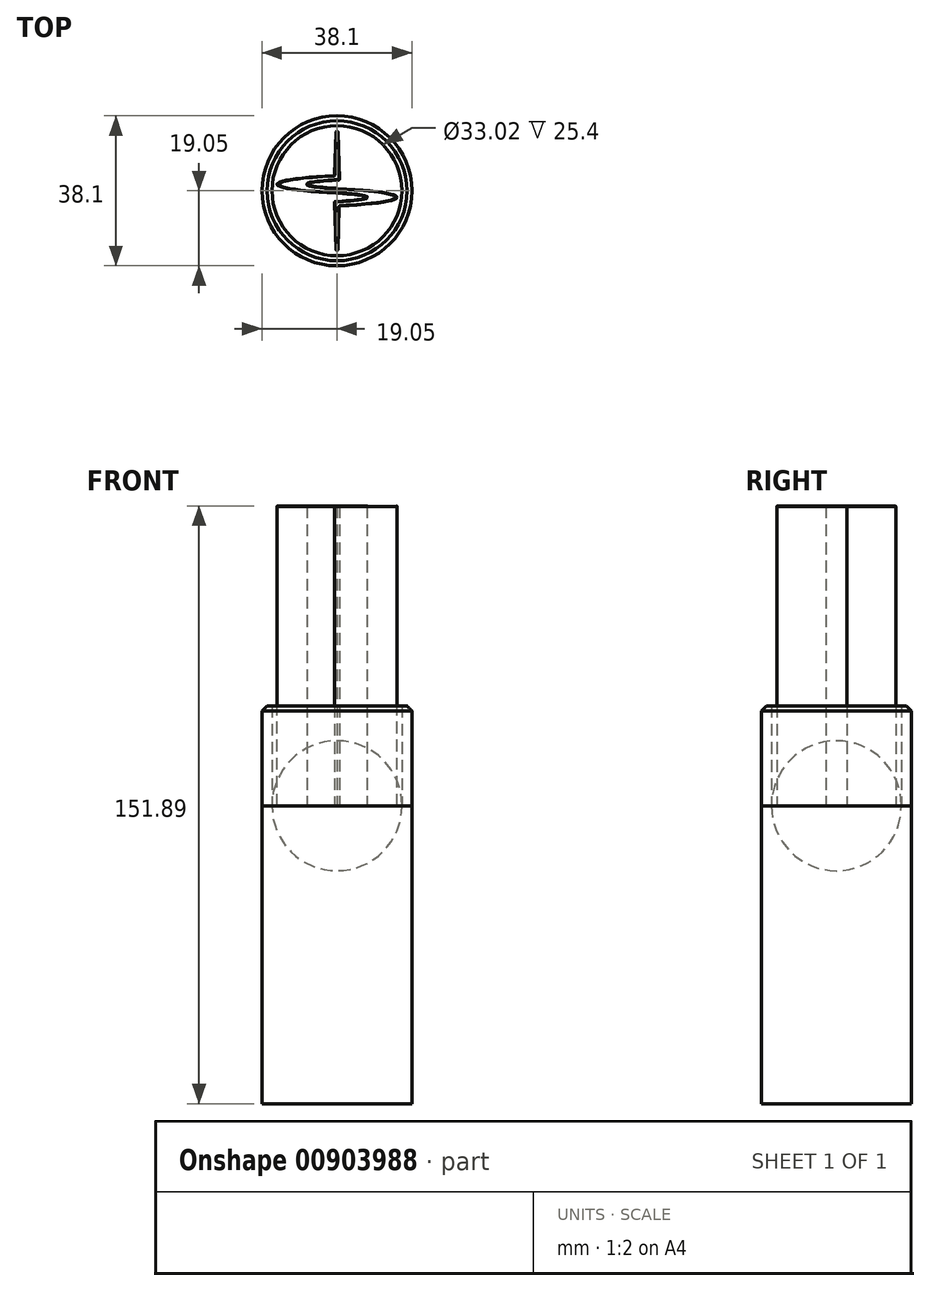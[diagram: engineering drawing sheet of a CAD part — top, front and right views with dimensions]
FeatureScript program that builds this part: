
annotation { "Feature Type Name" : "Feature", "Feature Type Description" : "" }
export const myFeature = defineFeature(function(context is Context, id is Id, definition is map)
    precondition{}
    {
        {
            var Q0;
            Q0=qCreatedBy(makeId("Top.planeOp"),FACE);
            var sketch = newSketch(context, id + "F0", { "sketchPlane" : qUnion([Q0])});
            skEllipticalArc(sketch, "E0", {});
            skEllipticalArc(sketch, "E1", {});
            skLineSegment(sketch, "E2", {"start": v(0, 0.6) * mm, "end": v(0, -0.6) * mm});
            skLineSegment(sketch, "E3", {"start": v(0, 3.92) * mm, "end": v(0, 2.71) * mm});
            const initialGuessF0  = {"E0": [0.0127, 0.0016577330848633332, -1, 0, 0.02794, 0.00254, 5.184250817664331, 1.0989344895152549], "E1": [0.0381, 0.0016577330848633332, -1, 0, 0.04572, 0.001905, 5.697499763722436, 0.5856855434571507]};
            skSetInitialGuess(sketch, initialGuessF0);
            skSolve(sketch);
        }
        {
            var Q0;
            Q0=qCreatedBy(makeId("Top.planeOp"),FACE);
            var sketch = newSketch(context, id + "F1", { "sketchPlane" : qUnion([Q0])});
            skLineSegment(sketch, "E4", {"start": v(-0.63, 2.71) * mm, "end": v(0.63, 2.71) * mm});
            skLineSegment(sketch, "E5", {"start": v(0.64, 2.71) * mm, "end": v(0, 23.03) * mm});
            skLineSegment(sketch, "E6", {"start": v(0, 23.03) * mm, "end": v(-0.64, 2.71) * mm});
            skSolve(sketch);
        }
        {
            var Q0;
            Q0=makeQuery(id+"F0.imprint","IMPRINT",FACE,{"disambiguationData":[TD([[makeQuery(id+"F0.imprint","IMPRINT",EDGE,{"derivedFrom":sQuery(id+"F0.wireOp",EDGE,"E0")}),1.0]])]});
            var Q1;
            Q1=makeQuery(id+"F1.imprint","IMPRINT",FACE,{"disambiguationData":[TD([[makeQuery(id+"F1.imprint","IMPRINT",EDGE,{"derivedFrom":sQuery(id+"F1.wireOp",EDGE,"E4")}),1.0]])]});
            extrude(context, id + "F2", {"entities" : qUnion([Q0, Q1]), "depth" : 76.2 * mm, "offsetDistance" : 25.4 * mm});
        }
        {
            var Q0;
            Q0=qCreatedBy(makeId("Front.planeOp"),FACE);
            var sketch = newSketch(context, id + "F3", { "sketchPlane" : qUnion([Q0])});
            skLineSegment(sketch, "E7", {"start": v(0, 85.95) * mm, "end": v(0, -92.06) * mm});
            skSolve(sketch);
        }
        {
            var Q0;
            Q0=makeQuery(id+"F2.opExtrude","SWEPT_BODY",BODY,{"disambiguationData":[OSD([sQuery(id+"F1.wireOp",EDGE,"E4"),sQuery(id+"F1.wireOp",EDGE,"E5"),sQuery(id+"F1.wireOp",EDGE,"E6")])]});
            var Q1;
            Q1=makeQuery(id+"F2.opExtrude","SWEPT_BODY",BODY,{"disambiguationData":[OSD([sQuery(id+"F0.wireOp",EDGE,"E0"),sQuery(id+"F0.wireOp",EDGE,"E1"),sQuery(id+"F0.wireOp",EDGE,"E2"),sQuery(id+"F0.wireOp",EDGE,"E3")])]});
            var Q2;
            Q2=sQuery(id+"F3.wireOp",EDGE,"E7");
            circularPattern(context, id + "F4", {"entities" : qUnion([Q0, Q1]), "axis" : qUnion([Q2]), "angle" : 360 * degree, "instanceCount" : 2, "equalSpace" : true});
        }
        {
            var Q0;
            Q0=makeQuery(id+"F2.opExtrude","SWEPT_BODY",BODY,{"disambiguationData":[OSD([sQuery(id+"F0.wireOp",EDGE,"E0"),sQuery(id+"F0.wireOp",EDGE,"E1"),sQuery(id+"F0.wireOp",EDGE,"E2"),sQuery(id+"F0.wireOp",EDGE,"E3")])]});
            var Q1;
            Q1=makeQuery(id+"F2.opExtrude","SWEPT_BODY",BODY,{"disambiguationData":[OSD([sQuery(id+"F1.wireOp",EDGE,"E4"),sQuery(id+"F1.wireOp",EDGE,"E5"),sQuery(id+"F1.wireOp",EDGE,"E6")])]});
            var Q2;
            Q2=makeQuery(id+"F4.opPattern","COPY",BODY,{"derivedFrom":makeQuery(id+"F2.opExtrude","SWEPT_BODY",BODY,{"disambiguationData":[OSD([sQuery(id+"F0.wireOp",EDGE,"E0"),sQuery(id+"F0.wireOp",EDGE,"E1"),sQuery(id+"F0.wireOp",EDGE,"E2"),sQuery(id+"F0.wireOp",EDGE,"E3")])]}),"instanceName":"1"});
            var Q3;
            Q3=makeQuery(id+"F4.opPattern","COPY",BODY,{"derivedFrom":makeQuery(id+"F2.opExtrude","SWEPT_BODY",BODY,{"disambiguationData":[OSD([sQuery(id+"F1.wireOp",EDGE,"E4"),sQuery(id+"F1.wireOp",EDGE,"E5"),sQuery(id+"F1.wireOp",EDGE,"E6")])]}),"instanceName":"1"});
            booleanBodies(context, id + "F5", {"operationType" : BooleanOperationType.UNION, "tools" : qUnion([Q0, Q1, Q2, Q3])});
        }
        {
            var Q0;
            Q0=makeQuery(id+"F2.opExtrude","SWEPT_EDGE",EDGE,{"disambiguationData":[OSD([sQuery(id+"F1.wireOp",EDGE,"E4"),sQuery(id+"F1.wireOp",EDGE,"E5")])]});
            var Q1;
            Q1=makeQuery(id+"F4.opPattern","COPY",EDGE,{"derivedFrom":makeQuery(id+"F2.opExtrude","SWEPT_EDGE",EDGE,{"disambiguationData":[OSD([sQuery(id+"F1.wireOp",EDGE,"E4"),sQuery(id+"F1.wireOp",EDGE,"E5")])]}),"instanceName":"1"});
            fillet(context, id + "F6", {"entities" : qUnion([Q0, Q1]), "radius" : 0.25 * mm, "tangentPropagation" : true, "allowEdgeOverflow" : false});
        }
        {
            var Q0;
            Q0=makeQuery(id+"F5.opBoolean","INTERSECT",EDGE,{"derivedFrom":[makeQuery(id+"F2.opExtrude","SWEPT_FACE",FACE,{"disambiguationData":[OSD([sQuery(id+"F0.wireOp",EDGE,"E0")])]}),makeQuery(id+"F2.opExtrude","SWEPT_FACE",FACE,{"disambiguationData":[OSD([sQuery(id+"F1.wireOp",EDGE,"E6")])]})]});
            var Q1;
            Q1=makeQuery(id+"F5.opBoolean","INTERSECT",EDGE,{"derivedFrom":[makeQuery(id+"F4.opPattern","COPY",FACE,{"derivedFrom":makeQuery(id+"F2.opExtrude","SWEPT_FACE",FACE,{"disambiguationData":[OSD([sQuery(id+"F0.wireOp",EDGE,"E0")])]}),"instanceName":"1"}),makeQuery(id+"F4.opPattern","COPY",FACE,{"derivedFrom":makeQuery(id+"F2.opExtrude","SWEPT_FACE",FACE,{"disambiguationData":[OSD([sQuery(id+"F1.wireOp",EDGE,"E6")])]}),"instanceName":"1"})]});
            fillet(context, id + "F7", {"entities" : qUnion([Q0, Q1]), "radius" : 0.25 * mm, "tangentPropagation" : true, "allowEdgeOverflow" : false});
        }
        {
            var Q0;
            Q0=makeQuery(id+"F2.opExtrude","SWEPT_EDGE",EDGE,{"disambiguationData":[OSD([sQuery(id+"F1.wireOp",EDGE,"E5"),sQuery(id+"F1.wireOp",EDGE,"E6")])]});
            var Q1;
            Q1=makeQuery(id+"F4.opPattern","COPY",EDGE,{"derivedFrom":makeQuery(id+"F2.opExtrude","SWEPT_EDGE",EDGE,{"disambiguationData":[OSD([sQuery(id+"F1.wireOp",EDGE,"E5"),sQuery(id+"F1.wireOp",EDGE,"E6")])]}),"instanceName":"1"});
            fillet(context, id + "F8", {"entities" : qUnion([Q0, Q1]), "radius" : 0.25 * mm, "tangentPropagation" : true, "allowEdgeOverflow" : false});
        }
        {
            var Q0;
            {var subQ0=sQuery(id+"F0.wireOp",EDGE,"E2");Q0=makeQuery(id+"F5.opBoolean","MERGE",EDGE,{"derivedFrom":[makeQuery(id+"F2.opExtrude","SWEPT_EDGE",EDGE,{"disambiguationData":[OSD([sQuery(id+"F0.wireOp",EDGE,"E1"),subQ0])]}),makeQuery(id+"F4.opPattern","COPY",EDGE,{"derivedFrom":makeQuery(id+"F2.opExtrude","SWEPT_EDGE",EDGE,{"disambiguationData":[OSD([sQuery(id+"F0.wireOp",EDGE,"E0"),subQ0])]}),"instanceName":"1"})]});}
            var Q1;
            {var subQ0=sQuery(id+"F0.wireOp",EDGE,"E2");Q1=makeQuery(id+"F5.opBoolean","MERGE",EDGE,{"derivedFrom":[makeQuery(id+"F2.opExtrude","SWEPT_EDGE",EDGE,{"disambiguationData":[OSD([sQuery(id+"F0.wireOp",EDGE,"E0"),subQ0])]}),makeQuery(id+"F4.opPattern","COPY",EDGE,{"derivedFrom":makeQuery(id+"F2.opExtrude","SWEPT_EDGE",EDGE,{"disambiguationData":[OSD([sQuery(id+"F0.wireOp",EDGE,"E1"),subQ0])]}),"instanceName":"1"})]});}
            fillet(context, id + "F9", {"entities" : qUnion([Q0, Q1]), "radius" : 25.4 * mm, "tangentPropagation" : true, "allowEdgeOverflow" : false});
        }
        {
            var Q0;
            Q0=makeQuery(id+"F4.opPattern","COPY",EDGE,{"derivedFrom":makeQuery(id+"F2.opExtrude","CAP_EDGE",EDGE,{"disambiguationData":[OSD([sQuery(id+"F0.wireOp",EDGE,"E1")])],"isStart":false}),"instanceName":"1"});
            var Q1;
            Q1=makeQuery(id+"F4.opPattern","COPY",EDGE,{"derivedFrom":makeQuery(id+"F2.opExtrude","CAP_EDGE",EDGE,{"disambiguationData":[OSD([sQuery(id+"F0.wireOp",EDGE,"E0")])],"isStart":false}),"instanceName":"1"});
            chamfer(context, id + "F10", {"entities" : qUnion([Q0, Q1]), "width" : 0.13 * mm, "tangentPropagation" : true});
        }
        {
            var Q0;
            Q0=qCreatedBy(makeId("Top.planeOp"),FACE);
            var sketch = newSketch(context, id + "F11", { "sketchPlane" : qUnion([Q0])});
            skCircle(sketch, "E8", {"center": v(0, 0) * mm, "radius": 19.05 * mm});
            skSolve(sketch);
        }
        {
            var Q0;
            Q0=makeQuery(id+"F11.imprint","IMPRINT",FACE,{"disambiguationData":[TD([[makeQuery(id+"F11.imprint","IMPRINT",EDGE,{"derivedFrom":sQuery(id+"F11.wireOp",EDGE,"E8")}),1.0]])]});
            extrude(context, id + "F12", {"entities" : qUnion([Q0]), "oppositeDirection" : true, "depth" : 75.7 * mm, "offsetDistance" : 25.4 * mm});
        }
        {
            var Q0;
            Q0=makeQuery(id+"F12.opExtrude","CAP_FACE",FACE,{"disambiguationData":[OSD([sQuery(id+"F11.wireOp",EDGE,"E8")])],"isStart":true});
            var sketch = newSketch(context, id + "F13", { "sketchPlane" : qUnion([Q0])});
            skCircle(sketch, "E9", {"center": v(0, 0) * mm, "radius": 19.05 * mm});
            skCircle(sketch, "E10", {"center": v(0, 0) * mm, "radius": 16.51 * mm});
            skSolve(sketch);
        }
        {
            var Q0;
            Q0=makeQuery(id+"F13.imprint","IMPRINT",FACE,{"disambiguationData":[TD([[makeQuery(id+"F13.imprint","IMPRINT",EDGE,{"derivedFrom":sQuery(id+"F13.wireOp",EDGE,"E9")}),1.0]])]});
            extrude(context, id + "F14", {"entities" : qUnion([Q0]), "depth" : 25.4 * mm, "offsetDistance" : 25.4 * mm});
        }
        {
            var Q0;
            Q0=makeQuery(id+"F14.opExtrude","CAP_EDGE",EDGE,{"disambiguationData":[OSD([sQuery(id+"F13.wireOp",EDGE,"E9")])],"isStart":false});
            chamfer(context, id + "F15", {"entities" : qUnion([Q0]), "width" : 1.27 * mm, "tangentPropagation" : true});
        }
        {
            var Q0;
            Q0=makeQuery(id+"F12.opExtrude","CAP_FACE",FACE,{"disambiguationData":[OSD([sQuery(id+"F11.wireOp",EDGE,"E8")])],"isStart":true});
            var sketch = newSketch(context, id + "F16", { "sketchPlane" : qUnion([Q0])});
            skArc(sketch, "E11", {"start": v(0, 16.51) * mm, "mid": v(-16.51, 0) * mm, "end": v(0, -16.51) * mm});
            skLineSegment(sketch, "E12", {"start": v(0, 0) * mm, "end": v(0, 16.51) * mm});
            skLineSegment(sketch, "E13", {"start": v(0, 0) * mm, "end": v(0, -16.51) * mm});
            skSolve(sketch);
        }
        {
            var Q0;
            Q0=makeQuery(id+"F16.imprint","IMPRINT",FACE,{"disambiguationData":[TD([[makeQuery(id+"F16.imprint","IMPRINT",EDGE,{"derivedFrom":sQuery(id+"F16.wireOp",EDGE,"E11")}),1.0]])]});
            var Q1;
            Q1=sQuery(id+"F16.wireOp",EDGE,"E12");
            revolve(context, id + "F17", {"surfaceOperationType" : NewSurfaceOperationType.NEW, "entities" : qUnion([Q0]), "axis" : qUnion([Q1]), "revolveType" : RevolveType.FULL});
        }
    });
